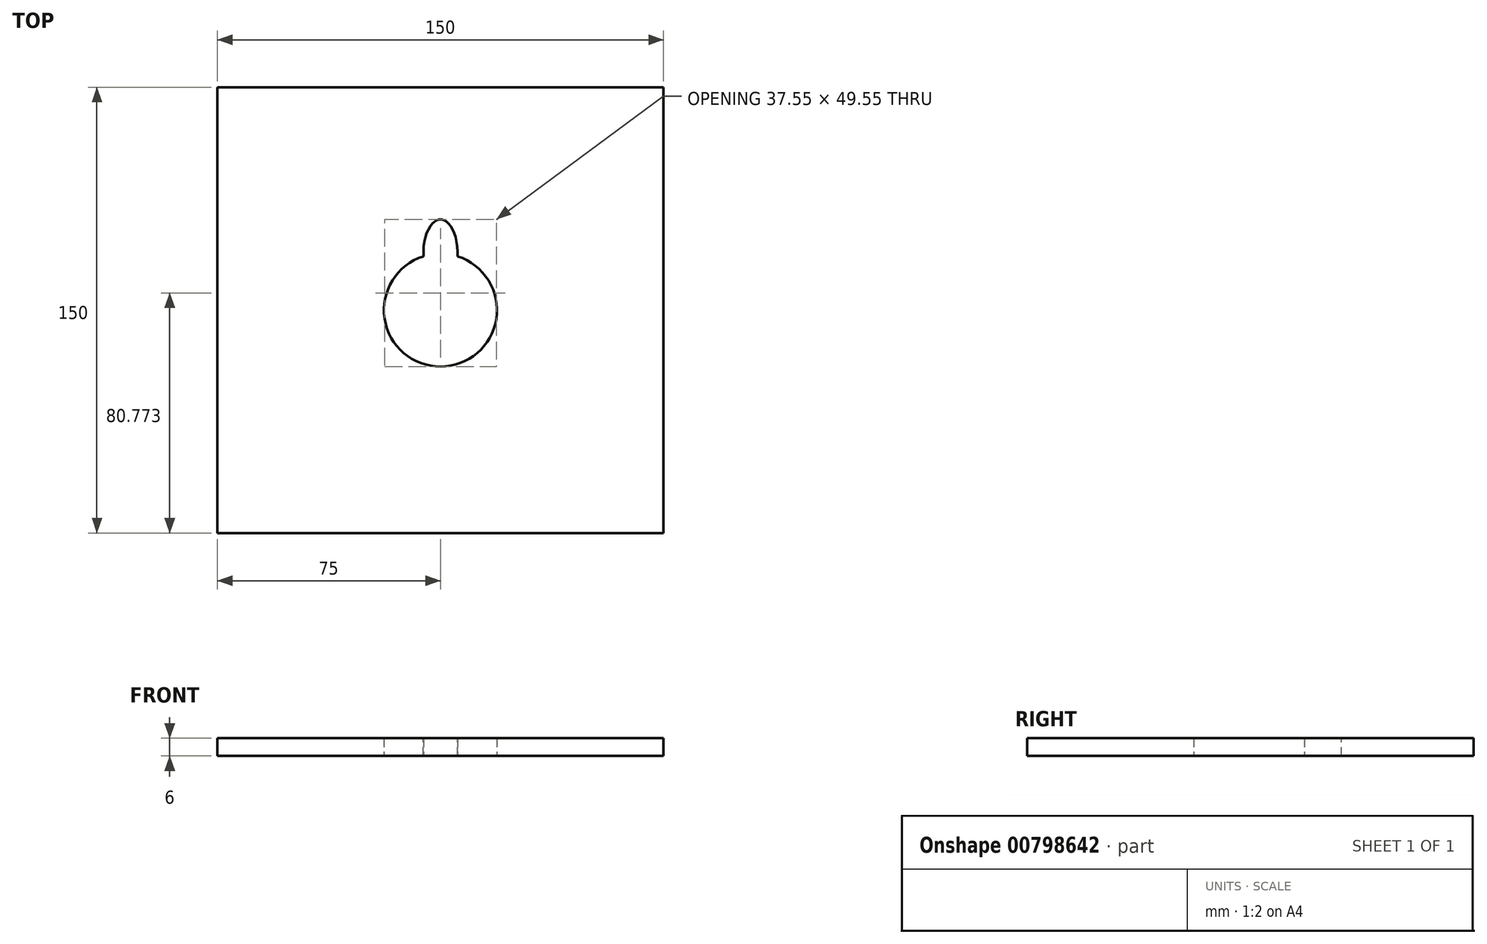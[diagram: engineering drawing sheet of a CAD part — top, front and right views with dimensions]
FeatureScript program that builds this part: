
annotation { "Feature Type Name" : "Feature", "Feature Type Description" : "" }
export const myFeature = defineFeature(function(context is Context, id is Id, definition is map)
    precondition{}
    {
        {
            var Q0;
            Q0=qCreatedBy(makeId("Top.planeOp"),FACE);
            var sketch = newSketch(context, id + "F0", { "sketchPlane" : qUnion([Q0])});
            skLineSegment(sketch, "E0.bottom", {"start": v(-75, 75) * mm, "end": v(75, 75) * mm});
            skLineSegment(sketch, "E0.top", {"start": v(-75, -75) * mm, "end": v(75, -75) * mm});
            skLineSegment(sketch, "E0.left", {"start": v(-75, 75) * mm, "end": v(-75, -75) * mm});
            skLineSegment(sketch, "E0.right", {"start": v(75, 75) * mm, "end": v(75, -75) * mm});
            skPoint(sketch, "E0.middle", {"position": v(0, 0) * mm});
            skArc(sketch, "E1", {"start": v(-5.73, 18.12) * mm, "mid": v(0, -19) * mm, "end": v(5.73, 18.12) * mm});
            skEllipticalArc(sketch, "E2", {});
            const initialGuessF0  = {"E2": [0, 0.019, 0, 1, 0.011545456659030635, 0.005747641575767963, 4.6356732139270616, 1.647512093252608]};
            skSetInitialGuess(sketch, initialGuessF0);
            skSolve(sketch);
        }
        {
            var Q0;
            Q0 = qSketchRegion(id + "F0", true);
            extrude(context, id + "F1", {"entities" : qUnion([Q0]), "depth" : 6 * mm, "offsetDistance" : 25 * mm});
        }
    });
